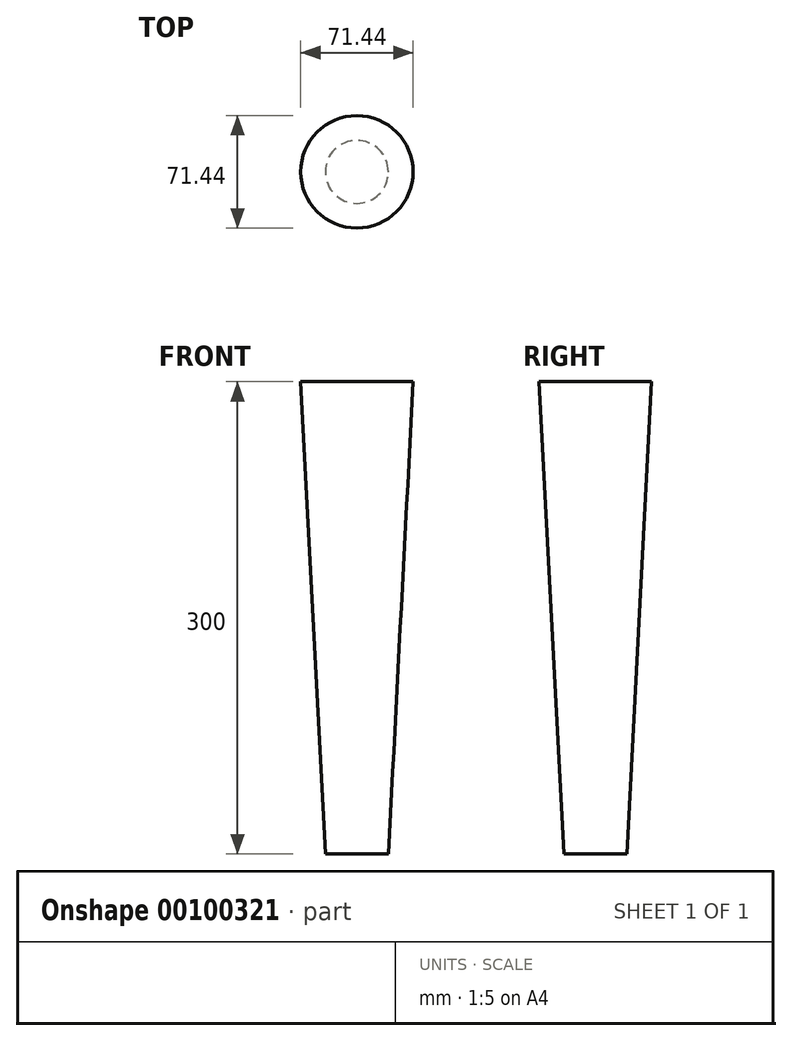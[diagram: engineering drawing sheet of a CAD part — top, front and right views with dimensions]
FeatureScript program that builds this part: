
annotation { "Feature Type Name" : "Feature", "Feature Type Description" : "" }
export const myFeature = defineFeature(function(context is Context, id is Id, definition is map)
    precondition{}
    {
        {
            var Q0;
            Q0=qCreatedBy(makeId("Top.planeOp"),FACE);
            var sketch = newSketch(context, id + "F0", { "sketchPlane" : qUnion([Q0])});
            skCircle(sketch, "E0", {"center": v(0, 0) * mm, "radius": 20 * mm});
            skSolve(sketch);
        }
        {
            var Q0;
            Q0 = qSketchRegion(id + "F0", true);
            extrude(context, id + "F1", {"entities" : qUnion([Q0]), "depth" : 300 * mm, "hasDraft" : true, "draftAngle" : 3 * degree});
        }
    });
